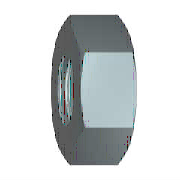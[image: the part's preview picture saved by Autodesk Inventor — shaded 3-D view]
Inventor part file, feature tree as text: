
AUTODESK INVENTOR PART (.ipt)
format: ipt  version: 2021 (Build 250183000, 183)  size: 164,352 bytes
history: native  units: mm (DEFAULTED — no unit token found)
features: other x5, chamfer x2, extrude x1, hole x1, plane x1
ambient origin geometry x7: Origin, YZ Plane, XZ Plane, X Axis, Y Axis, Z Axis, Center Point
bodies: Solid1 (feature_tree)
feature tree (10):
  extrude  "Corpo"  Depth=8.082904mm
  other  "Chanfrar1"
  hole  "Rosca"  [1 undecoded]
  chamfer  "Chanfrar2"  [1 undecoded]
  chamfer  "Chanfrar3"  Angle=30.0deg  [1 undecoded]
  other  "Work Axis1"
  plane  "Work Plane1"
  other  "Rascunho1"
  other  "Rascunho2"
  other  "Rascunho3"
note: 3 required parameter values undecoded (feature->parameter linkage not recoverable at this tier; creation-order binding heuristic only, values carry confidence <= 0.55)
